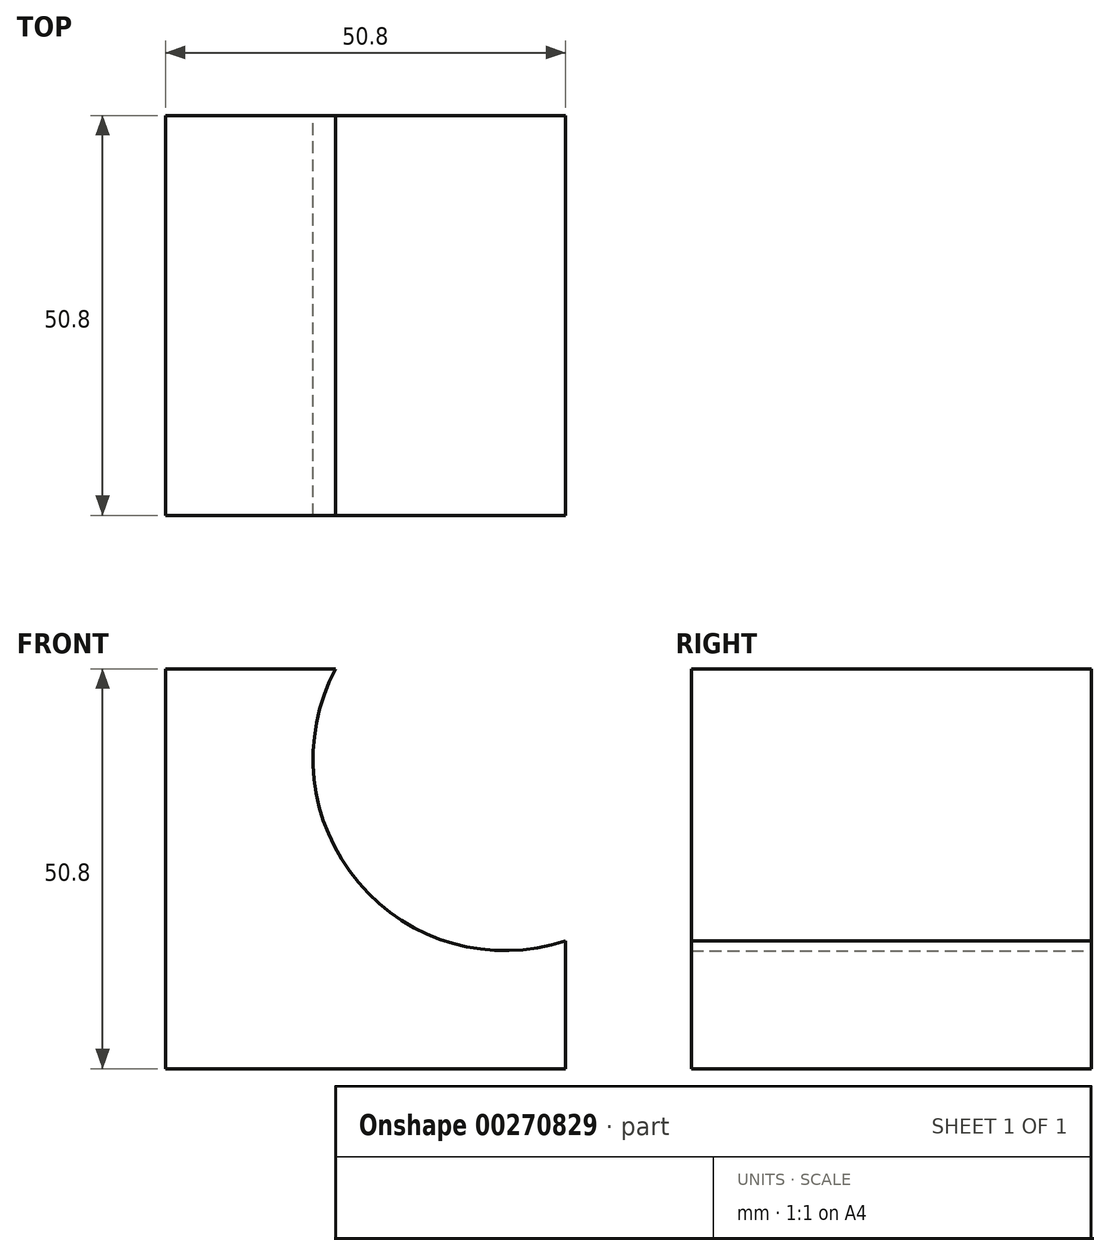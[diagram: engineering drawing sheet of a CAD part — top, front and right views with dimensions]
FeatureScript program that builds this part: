
annotation { "Feature Type Name" : "Feature", "Feature Type Description" : "" }
export const myFeature = defineFeature(function(context is Context, id is Id, definition is map)
    precondition{}
    {
        {
            var Q0;
            Q0=qCreatedBy(makeId("Front.planeOp"),FACE);
            var sketch = newSketch(context, id + "F0", { "sketchPlane" : qUnion([Q0])});
            skLineSegment(sketch, "E0", {"start": v(0, 0) * mm, "end": v(-50.8, 0) * mm});
            skLineSegment(sketch, "E1", {"start": v(-50.8, 0) * mm, "end": v(-50.8, 50.8) * mm});
            skLineSegment(sketch, "E2", {"start": v(-50.8, 50.8) * mm, "end": v(-29.22, 50.8) * mm});
            skLineSegment(sketch, "E3", {"start": v(0, 0) * mm, "end": v(0, 16.23) * mm});
            skArc(sketch, "E4", {"start": v(-29.22, 50.8) * mm, "mid": v(-26.3, 23.63) * mm, "end": v(0, 16.23) * mm});
            skSolve(sketch);
        }
        {
            var Q0;
            Q0 = qSketchRegion(id + "F0", true);
            extrude(context, id + "F1", {"entities" : qUnion([Q0]), "depth" : 50.8 * mm});
        }
    });
